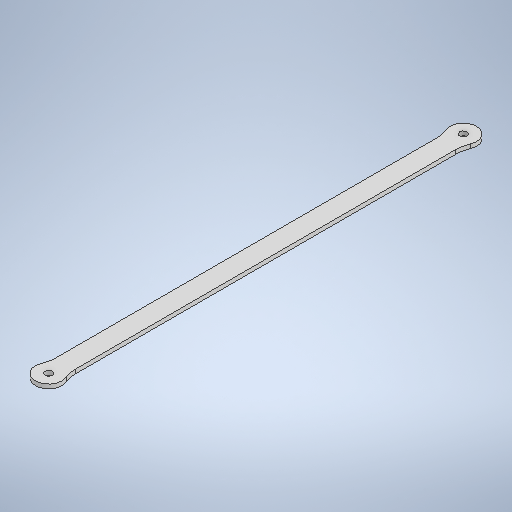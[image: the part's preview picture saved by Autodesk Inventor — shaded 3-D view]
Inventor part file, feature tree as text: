
AUTODESK INVENTOR PART (.ipt)
format: ipt  version: 2025.2 (Build 292293000, 293)  size: 282,624 bytes
history: native  units: in
note: dims shown in document units (in); Inventor stores cm internally (conversion verified against a paired STEP export)
features: extrude x2, sketch x2
ambient origin geometry x8: Origin, YZ Plane, XZ Plane, XY Plane, X Axis, Y Axis, Z Axis, Center Point
bodies: Solid1 (feature_tree)
feature tree (4):
  extrude  "Extrusion1"  Depth=0.1575in
  extrude  "Extrusion2"  TaperAngle=0.0deg  [1 undecoded]
  sketch  "Sketch1"  dims[d0=0.4291in d4=0.1575in]
  sketch  "Sketch2"  dims[d5=0.1575in d6=0.0in d7=0.4291in d8=6.6929in d9=0.0in d10=0.2756in d12=0.1575in d13=0.2756in d14=0.0669in d15=0.0in d16=0.1181in d17=0.1181in d18=0.0669in d19=0.0in]
note: 1 required parameter value undecoded (feature->parameter linkage not recoverable at this tier; creation-order binding heuristic only, values carry confidence <= 0.55)
